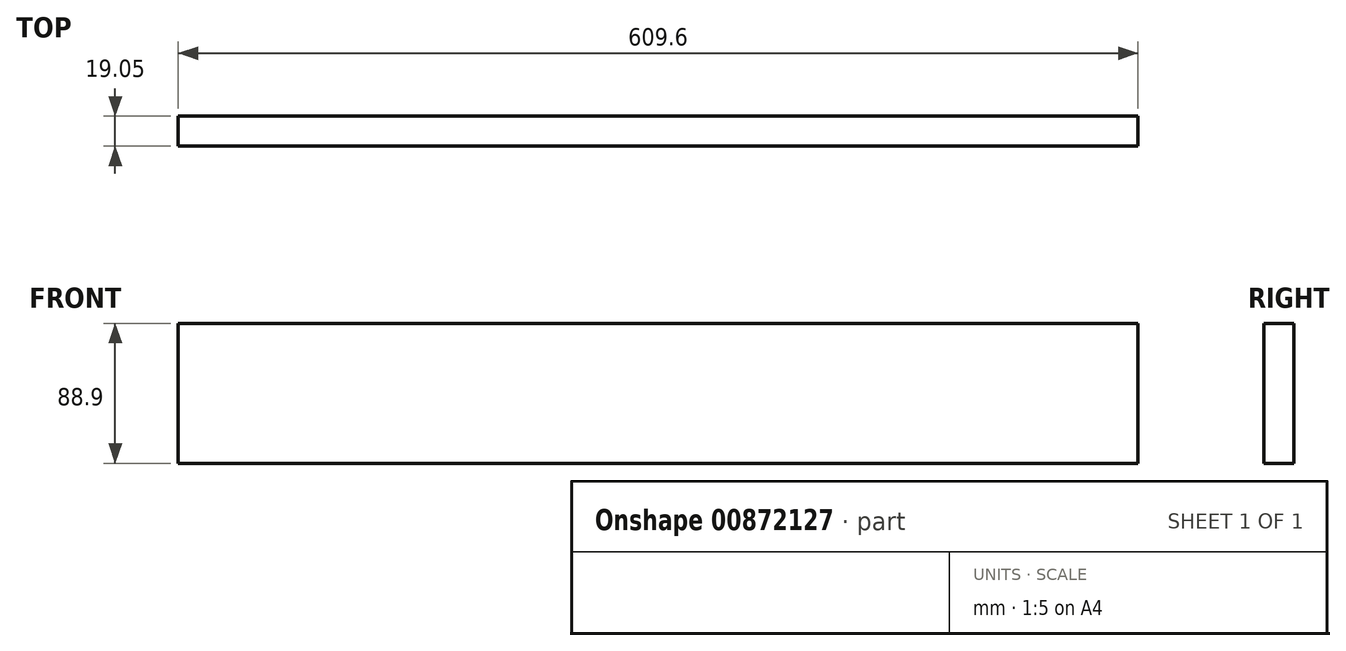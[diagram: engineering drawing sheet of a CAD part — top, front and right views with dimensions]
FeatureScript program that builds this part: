
annotation { "Feature Type Name" : "Feature", "Feature Type Description" : "" }
export const myFeature = defineFeature(function(context is Context, id is Id, definition is map)
    precondition{}
    {
        {
            var Q0;
            Q0=qCreatedBy(makeId("Front.planeOp"),FACE);
            var sketch = newSketch(context, id + "F0", { "sketchPlane" : qUnion([Q0])});
            skLineSegment(sketch, "E0.bottom", {"start": v(0, 0) * mm, "end": v(-609.6, 0) * mm});
            skLineSegment(sketch, "E0.top", {"start": v(0, 88.9) * mm, "end": v(-609.6, 88.9) * mm});
            skLineSegment(sketch, "E0.left", {"start": v(0, 0) * mm, "end": v(0, 88.9) * mm});
            skLineSegment(sketch, "E0.right", {"start": v(-609.6, 0) * mm, "end": v(-609.6, 88.9) * mm});
            skSolve(sketch);
        }
        {
            var Q0;
            Q0=makeQuery(id+"F0.imprint","IMPRINT",FACE,{"disambiguationData":[TD([[makeQuery(id+"F0.imprint","IMPRINT",EDGE,{"derivedFrom":sQuery(id+"F0.wireOp",EDGE,"E0.bottom")}),-1.0]])]});
            extrude(context, id + "F1", {"entities" : qUnion([Q0]), "depth" : 19.05 * mm, "offsetDistance" : 25.4 * mm});
        }
    });
